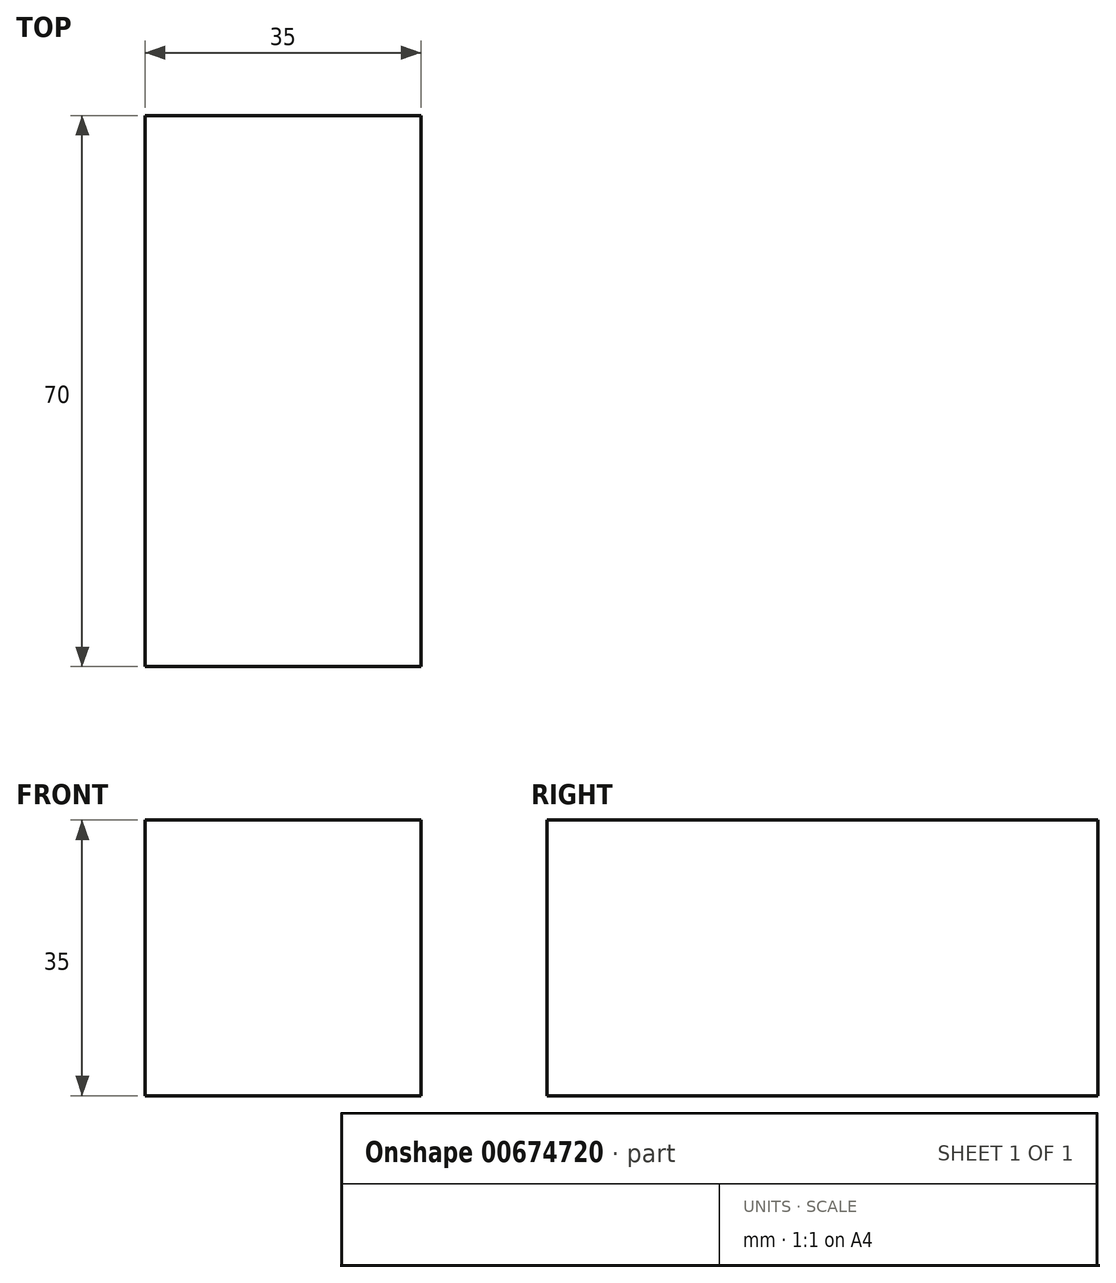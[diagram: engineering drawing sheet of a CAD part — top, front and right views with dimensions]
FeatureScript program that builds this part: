
annotation { "Feature Type Name" : "Feature", "Feature Type Description" : "" }
export const myFeature = defineFeature(function(context is Context, id is Id, definition is map)
    precondition{}
    {
        {
            var Q0;
            Q0=qCreatedBy(makeId("Front.planeOp"),FACE);
            var sketch = newSketch(context, id + "F0", { "sketchPlane" : qUnion([Q0])});
            skLineSegment(sketch, "E0.bottom", {"start": v(0, 0) * mm, "end": v(35, 0) * mm});
            skLineSegment(sketch, "E0.top", {"start": v(0, 35) * mm, "end": v(35, 35) * mm});
            skLineSegment(sketch, "E0.left", {"start": v(0, 0) * mm, "end": v(0, 35) * mm});
            skLineSegment(sketch, "E0.right", {"start": v(35, 0) * mm, "end": v(35, 35) * mm});
            skSolve(sketch);
        }
        {
            var Q0;
            Q0=makeQuery(id+"F0.imprint","IMPRINT",FACE,{"disambiguationData":[TD([[makeQuery(id+"F0.imprint","IMPRINT",EDGE,{"derivedFrom":sQuery(id+"F0.wireOp",EDGE,"E0.bottom")}),1.0]])]});
            extrude(context, id + "F1", {"entities" : qUnion([Q0]), "depth" : 70 * mm, "offsetDistance" : 25 * mm});
        }
    });
